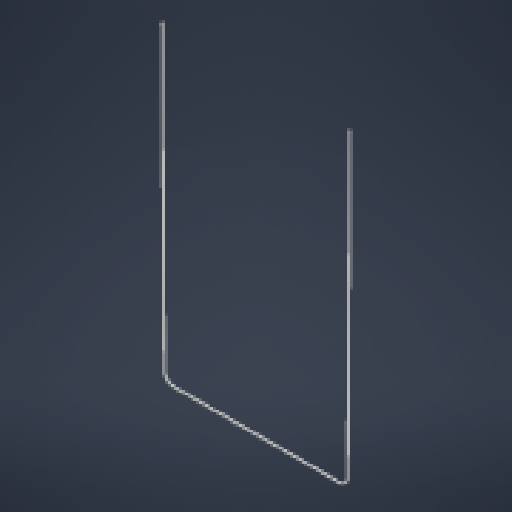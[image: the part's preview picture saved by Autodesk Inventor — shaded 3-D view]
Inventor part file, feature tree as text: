
AUTODESK INVENTOR PART (.ipt)
format: ipt  version: 2024 (Build 280153000, 153)  size: 156,672 bytes
history: native  units: in
note: dims shown in document units (in); Inventor stores cm internally (conversion verified against a paired STEP export)
features: sketch x2, plane x1, sweep x1
ambient origin geometry x8: Origin, YZ Plane, XZ Plane, XY Plane, X Axis, Y Axis, Z Axis, Center Point
bodies: Body1 (feature_tree)
feature tree (4):
  sketch  "Sketch3"  dims[d13=9.8in d18=0.5in]
  plane  "Work Plane2"
  sweep  "Sweep2"
  sketch  "Sketch4"  dims[d19=0.1181in d20=0.0in d21=0.0in d23=0.1in d24=0.1in d25=1.0in d26=1.0in]
